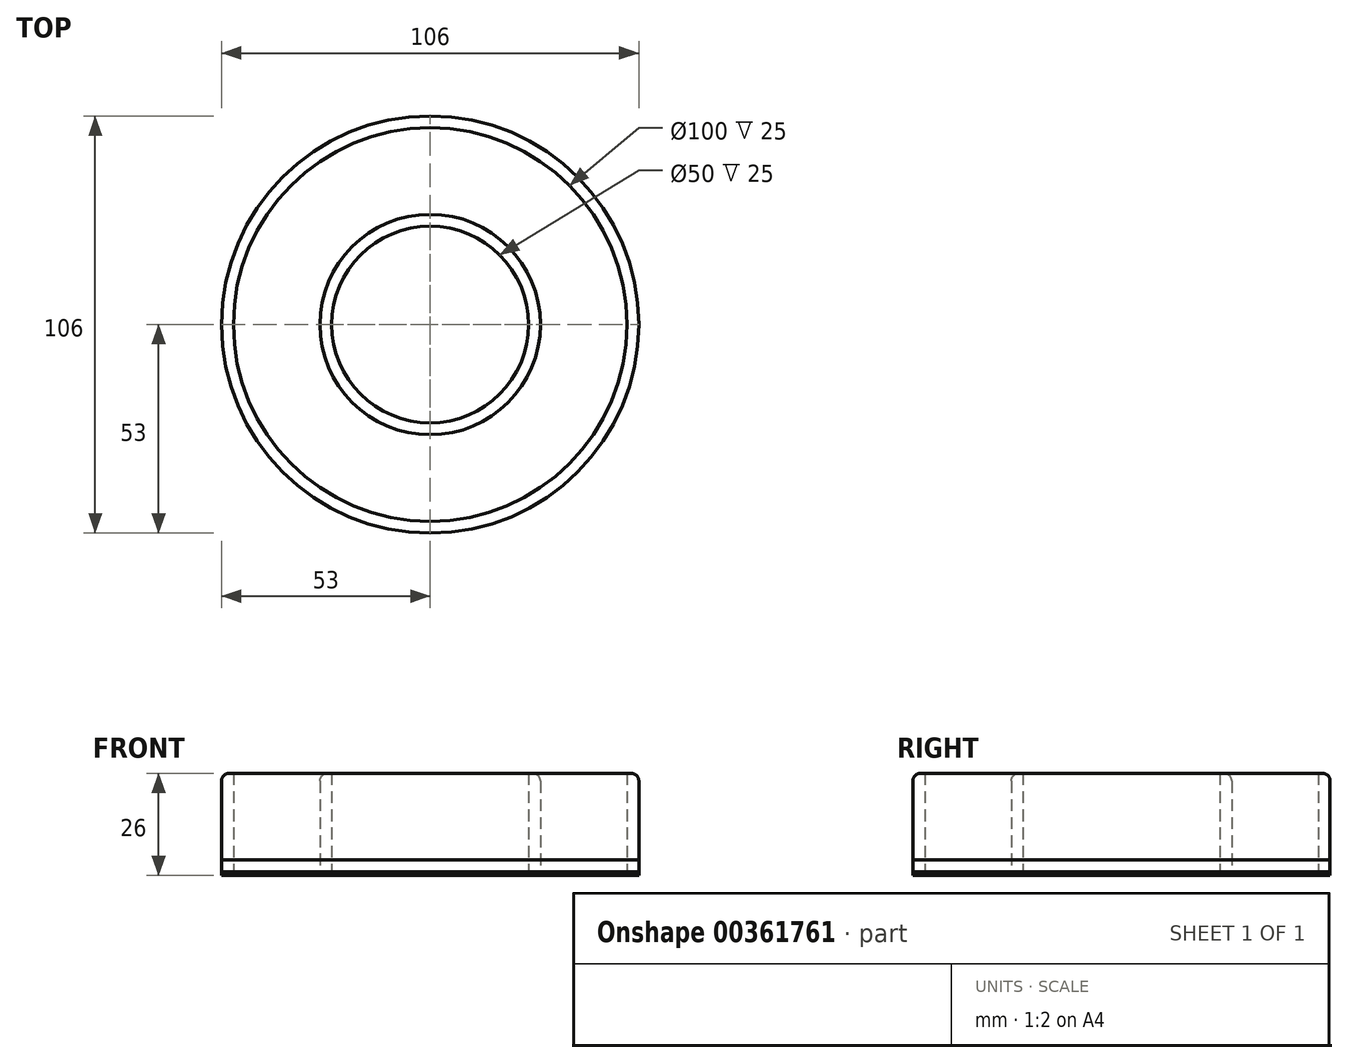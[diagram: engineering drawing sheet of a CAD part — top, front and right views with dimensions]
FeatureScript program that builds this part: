
annotation { "Feature Type Name" : "Feature", "Feature Type Description" : "" }
export const myFeature = defineFeature(function(context is Context, id is Id, definition is map)
    precondition{}
    {
        {
            var Q0;
            Q0=qCreatedBy(makeId("Top.planeOp"),FACE);
            var sketch = newSketch(context, id + "F0", { "sketchPlane" : qUnion([Q0])});
            skCircle(sketch, "E0", {"center": v(0, 0) * mm, "radius": 50 * mm});
            skCircle(sketch, "E1", {"center": v(0, 0) * mm, "radius": 53 * mm});
            skCircle(sketch, "E2", {"center": v(0, 0) * mm, "radius": 28 * mm});
            skCircle(sketch, "E3", {"center": v(0, 0) * mm, "radius": 25 * mm});
            skSolve(sketch);
        }
        {
            var Q0;
            Q0=makeQuery(id+"F0.imprint","IMPRINT",FACE,{"disambiguationData":[TD([[makeQuery(id+"F0.imprint","IMPRINT",EDGE,{"derivedFrom":sQuery(id+"F0.wireOp",EDGE,"E0")}),-1.0]])]});
            var Q1;
            Q1=makeQuery(id+"F0.imprint","IMPRINT",FACE,{"disambiguationData":[TD([[makeQuery(id+"F0.imprint","IMPRINT",EDGE,{"derivedFrom":sQuery(id+"F0.wireOp",EDGE,"E2")}),1.0]])]});
            extrude(context, id + "F1", {"entities" : qUnion([Q0, Q1]), "depth" : 25 * mm});
        }
        {
            var Q0;
            Q0=makeQuery(id+"F0.imprint","IMPRINT",FACE,{"disambiguationData":[TD([[makeQuery(id+"F0.imprint","IMPRINT",EDGE,{"derivedFrom":sQuery(id+"F0.wireOp",EDGE,"E0")}),-1.0]])]});
            var Q1;
            Q1=makeQuery(id+"F0.imprint","IMPRINT",FACE,{"disambiguationData":[TD([[makeQuery(id+"F0.imprint","IMPRINT",EDGE,{"derivedFrom":sQuery(id+"F0.wireOp",EDGE,"E0")}),1.0]])]});
            var Q2;
            Q2=makeQuery(id+"F0.imprint","IMPRINT",FACE,{"disambiguationData":[TD([[makeQuery(id+"F0.imprint","IMPRINT",EDGE,{"derivedFrom":sQuery(id+"F0.wireOp",EDGE,"E3")}),1.0]])]});
            var Q3;
            Q3=makeQuery(id+"F0.imprint","IMPRINT",FACE,{"disambiguationData":[TD([[makeQuery(id+"F0.imprint","IMPRINT",EDGE,{"derivedFrom":sQuery(id+"F0.wireOp",EDGE,"E2")}),1.0]])]});
            extrude(context, id + "F2", {"entities" : qUnion([Q0, Q1, Q2, Q3]), "oppositeDirection" : true, "depth" : 4 * mm});
        }
        {
            var Q0;
            Q0=makeQuery(id+"F2.opExtrude","SWEPT_BODY",BODY,{"disambiguationData":[OSD([sQuery(id+"F0.wireOp",EDGE,"E1")])]});
            var Q1;
            Q1=qCreatedBy(makeId("Top.planeOp"),FACE);
            transform(context, id + "F3", {"entities" : qUnion([Q0]), "transformType" : TransformType.TRANSLATION_DISTANCE, "transformDirection" : qUnion([Q1]), "distance" : 3 * mm, "makeCopy" : false});
        }
        {
            var Q0;
            Q0=makeQuery(id+"F1.opExtrude","CAP_EDGE",EDGE,{"disambiguationData":[OSD([sQuery(id+"F0.wireOp",EDGE,"E1")])],"isStart":false});
            var Q1;
            Q1=makeQuery(id+"F1.opExtrude","CAP_EDGE",EDGE,{"disambiguationData":[OSD([sQuery(id+"F0.wireOp",EDGE,"E2")])],"isStart":false});
            fillet(context, id + "F4", {"entities" : qUnion([Q0, Q1]), "radius" : 2 * mm, "tangentPropagation" : true, "allowEdgeOverflow" : false});
        }
    });
